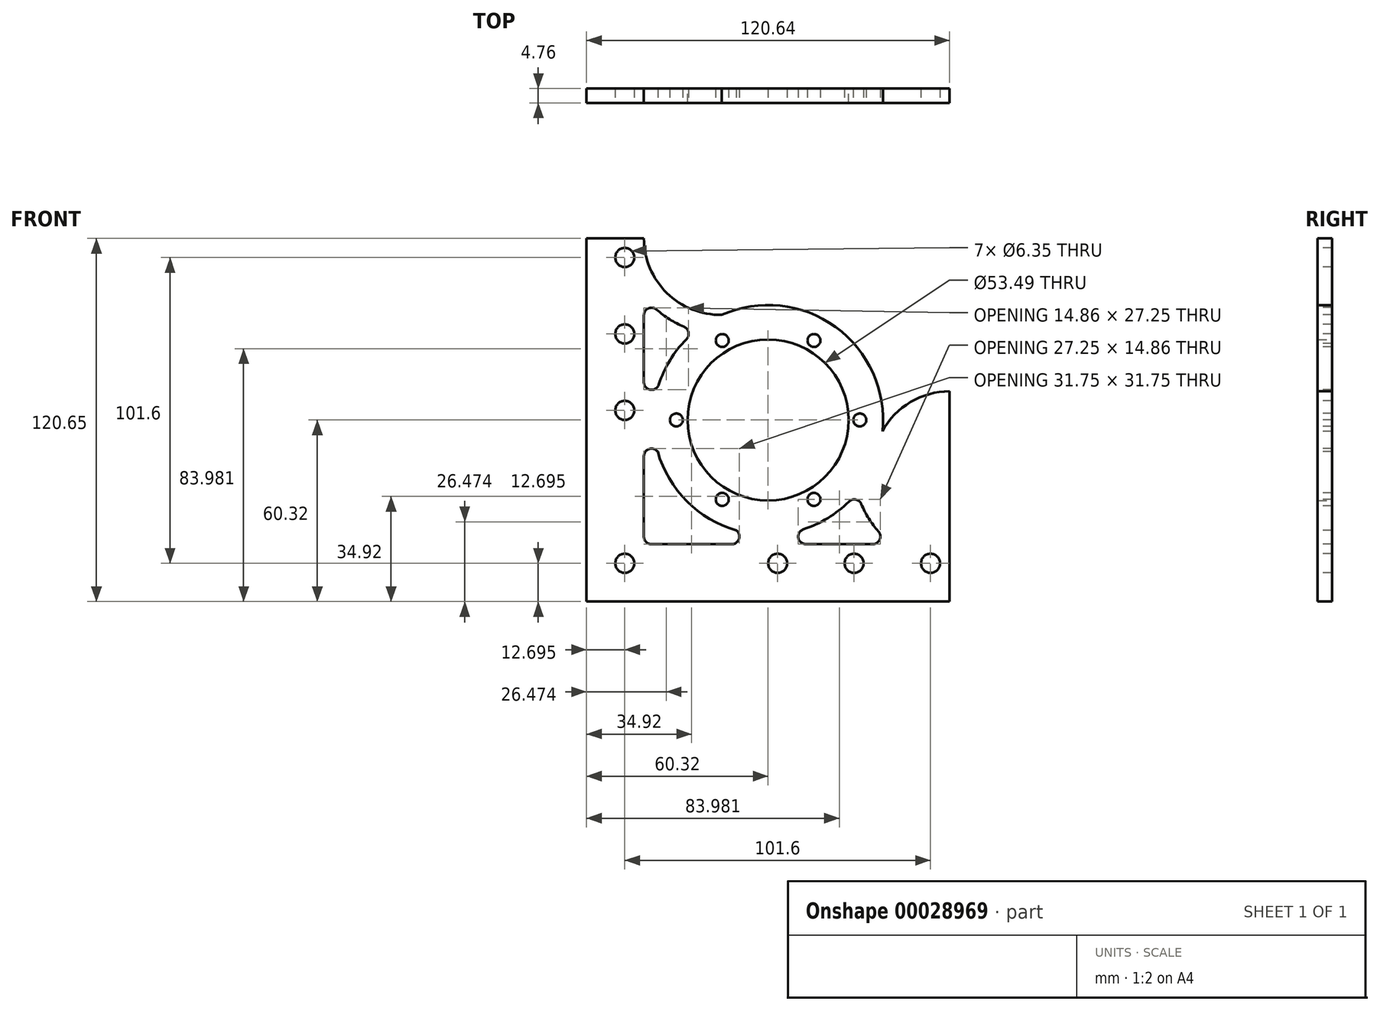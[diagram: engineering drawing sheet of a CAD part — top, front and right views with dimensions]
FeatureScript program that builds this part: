
annotation { "Feature Type Name" : "Feature", "Feature Type Description" : "" }
export const myFeature = defineFeature(function(context is Context, id is Id, definition is map)
    precondition{}
    {
        {
            var Q0;
            Q0=qCreatedBy(makeId("Front.planeOp"),FACE);
            var sketch = newSketch(context, id + "F0", { "sketchPlane" : qUnion([Q0])});
            skLineSegment(sketch, "E0.rect.bottom", {"start": v(60.32, -60.33) * mm, "end": v(-60.33, -60.33) * mm});
            skLineSegment(sketch, "E0.rect.top", {"start": v(60.33, 60.33) * mm, "end": v(-60.32, 60.33) * mm});
            skLineSegment(sketch, "E0.rect.left", {"start": v(60.32, -60.33) * mm, "end": v(60.33, 60.32) * mm});
            skLineSegment(sketch, "E0.rect.right", {"start": v(-60.33, -60.33) * mm, "end": v(-60.32, 60.32) * mm});
            skPoint(sketch, "E0.rect.middle", {"position": v(0, 0) * mm});
            skCircle(sketch, "E1", {"center": v(0, 0) * mm, "radius": 26.75 * mm});
            skSolve(sketch);
        }
        {
            var Q0;
            Q0=makeQuery(id+"F0.imprint","IMPRINT",FACE,{"disambiguationData":[TD([[makeQuery(id+"F0.imprint","IMPRINT",EDGE,{"derivedFrom":sQuery(id+"F0.wireOp",EDGE,"E0.rect.bottom")}),-1.0]])]});
            extrude(context, id + "F1", {"entities" : qUnion([Q0]), "depth" : 4.76 * mm});
        }
        {
            var Q0;
            Q0=makeQuery(id+"F1.opExtrude","CAP_FACE",FACE,{"disambiguationData":[OSD([sQuery(id+"F0.wireOp",EDGE,"E0.rect.bottom"),sQuery(id+"F0.wireOp",EDGE,"E0.rect.top"),sQuery(id+"F0.wireOp",EDGE,"E0.rect.left"),sQuery(id+"F0.wireOp",EDGE,"E0.rect.right"),sQuery(id+"F0.wireOp",EDGE,"E1")])],"isStart":false});
            var sketch = newSketch(context, id + "F2", { "sketchPlane" : qUnion([Q0])});
            skLineSegment(sketch, "E2", {"start": v(-47.63, 77.95) * mm, "end": v(-47.63, -81.86) * mm});
            skLineSegment(sketch, "E3", {"start": v(-79.01, -47.63) * mm, "end": v(89.4, -47.63) * mm});
            skPoint(sketch, "E4", {"position": v(-47.63, -47.63) * mm});
            skPoint(sketch, "E5", {"position": v(3.17, -47.63) * mm});
            skPoint(sketch, "E6", {"position": v(28.58, -47.63) * mm});
            skPoint(sketch, "E7", {"position": v(53.98, -47.63) * mm});
            skPoint(sketch, "E8", {"position": v(-47.63, 3.17) * mm});
            skPoint(sketch, "E9", {"position": v(-47.63, 28.57) * mm});
            skPoint(sketch, "E10", {"position": v(-47.63, 53.97) * mm});
            skSolve(sketch);
        }
        {
            var Q0;
            Q0=sQuery(id+"F2.wireOp",VERTEX,"E10");
            var Q1;
            Q1=sQuery(id+"F2.wireOp",VERTEX,"E9");
            var Q2;
            Q2=sQuery(id+"F2.wireOp",VERTEX,"E8");
            var Q3;
            Q3=sQuery(id+"F2.wireOp",VERTEX,"E4");
            var Q4;
            Q4=sQuery(id+"F2.wireOp",VERTEX,"E5");
            var Q5;
            Q5=sQuery(id+"F2.wireOp",VERTEX,"E6");
            var Q6;
            Q6=sQuery(id+"F2.wireOp",VERTEX,"E7");
            var Q7;
            Q7=makeQuery(id+"F1.opExtrude","SWEPT_BODY",BODY,{"disambiguationData":[OSD([sQuery(id+"F0.wireOp",EDGE,"E0.rect.bottom"),sQuery(id+"F0.wireOp",EDGE,"E0.rect.top"),sQuery(id+"F0.wireOp",EDGE,"E0.rect.left"),sQuery(id+"F0.wireOp",EDGE,"E0.rect.right"),sQuery(id+"F0.wireOp",EDGE,"E1")])]});
            hole(context, id + "F3", {"style" : HoleStyle.SIMPLE, "holeDiameter" : 6.35 * mm, "endStyle" : HoleEndStyle.THROUGH, "locations" : qUnion([Q0, Q1, Q2, Q3, Q4, Q5, Q6]), "scope" : qUnion([Q7])});
        }
        {
            var Q0;
            Q0=makeQuery(id+"F1.opExtrude","CAP_FACE",FACE,{"disambiguationData":[OSD([sQuery(id+"F0.wireOp",EDGE,"E0.rect.bottom"),sQuery(id+"F0.wireOp",EDGE,"E0.rect.top"),sQuery(id+"F0.wireOp",EDGE,"E0.rect.left"),sQuery(id+"F0.wireOp",EDGE,"E0.rect.right"),sQuery(id+"F0.wireOp",EDGE,"E1")])],"isStart":false});
            var sketch = newSketch(context, id + "F4", { "sketchPlane" : qUnion([Q0])});
            skCircle(sketch, "E11", {"center": v(0, 0) * mm, "radius": 30.48 * mm});
            skCircle(sketch, "E12.cCircle", {"center": v(0, 0) * mm, "radius": 30.48 * mm, "construction": true});
            skLineSegment(sketch, "E12.0", {"start": v(30.48, 0) * mm, "end": v(15.24, -26.4) * mm});
            skLineSegment(sketch, "E12.1", {"start": v(15.24, -26.4) * mm, "end": v(-15.24, -26.4) * mm});
            skLineSegment(sketch, "E12.2", {"start": v(-15.24, -26.4) * mm, "end": v(-30.48, 0) * mm});
            skLineSegment(sketch, "E12.3", {"start": v(-30.48, 0) * mm, "end": v(-15.24, 26.4) * mm});
            skLineSegment(sketch, "E12.4", {"start": v(-15.24, 26.4) * mm, "end": v(15.24, 26.4) * mm});
            skLineSegment(sketch, "E12.5", {"start": v(15.24, 26.4) * mm, "end": v(30.48, 0) * mm});
            skSolve(sketch);
        }
        {
            var Q0;
            Q0=sQuery(id+"F4.wireOp",VERTEX,"E12.4.end");
            var Q1;
            Q1=sQuery(id+"F4.wireOp",VERTEX,"E12.5.end");
            var Q2;
            Q2=sQuery(id+"F4.wireOp",VERTEX,"E12.0.end");
            var Q3;
            Q3=sQuery(id+"F4.wireOp",VERTEX,"E12.1.end");
            var Q4;
            Q4=sQuery(id+"F4.wireOp",VERTEX,"E12.2.end");
            var Q5;
            Q5=sQuery(id+"F4.wireOp",VERTEX,"E12.3.end");
            var Q6;
            Q6=makeQuery(id+"F1.opExtrude","SWEPT_BODY",BODY,{"disambiguationData":[OSD([sQuery(id+"F0.wireOp",EDGE,"E0.rect.bottom"),sQuery(id+"F0.wireOp",EDGE,"E0.rect.top"),sQuery(id+"F0.wireOp",EDGE,"E0.rect.left"),sQuery(id+"F0.wireOp",EDGE,"E0.rect.right"),sQuery(id+"F0.wireOp",EDGE,"E1")])]});
            hole(context, id + "F5", {"style" : HoleStyle.SIMPLE, "holeDiameter" : 4.3 * mm, "endStyle" : HoleEndStyle.THROUGH, "locations" : qUnion([Q0, Q1, Q2, Q3, Q4, Q5]), "scope" : qUnion([Q6])});
        }
        {
            var Q0;
            Q0=makeQuery(id+"F1.opExtrude","CAP_FACE",FACE,{"disambiguationData":[OSD([sQuery(id+"F0.wireOp",EDGE,"E0.rect.bottom"),sQuery(id+"F0.wireOp",EDGE,"E0.rect.top"),sQuery(id+"F0.wireOp",EDGE,"E0.rect.left"),sQuery(id+"F0.wireOp",EDGE,"E0.rect.right"),sQuery(id+"F0.wireOp",EDGE,"E1")])],"isStart":false});
            var sketch = newSketch(context, id + "F6", { "sketchPlane" : qUnion([Q0])});
            skLineSegment(sketch, "E13.0", {"start": v(-41.28, -41.28) * mm, "end": v(41.28, -41.28) * mm});
            skLineSegment(sketch, "E13.1", {"start": v(-41.28, 41.28) * mm, "end": v(-41.28, -41.28) * mm});
            skLineSegment(sketch, "E13.2", {"start": v(41.28, 41.28) * mm, "end": v(-41.28, 41.28) * mm});
            skLineSegment(sketch, "E13.3", {"start": v(41.28, -41.28) * mm, "end": v(41.28, 41.28) * mm});
            skCircle(sketch, "E14.0", {"center": v(0, 0) * mm, "radius": 38.18 * mm});
            skArc(sketch, "E15", {"start": v(-3.78, 37.99) * mm, "mid": v(-22.34, 84.89) * mm, "end": v(-15.4, 34.93) * mm});
            skArc(sketch, "E16", {"start": v(34.93, -15.4) * mm, "mid": v(84.89, -22.34) * mm, "end": v(37.99, -3.78) * mm});
            skSolve(sketch);
        }
        {
            var Q0;
            {var subQ1=sQuery(id+"F6.wireOp",EDGE,"E15");var subQ4=sQuery(id+"F6.wireOp",EDGE,"E13.2");var subQ6=makeQuery(id+"F6.imprint","INTERSECT",VERTEX,{"disambiguationData":[OD(0.0)],"derivedFrom":[subQ4,subQ1]});Q0=makeQuery(id+"F6.imprint","IMPRINT",FACE,{"disambiguationData":[TD([[makeQuery(id+"F6.imprint","IMPRINT",EDGE,{"disambiguationData":[TD([[subQ6,-1.0]])],"derivedFrom":subQ4}),-1.0]])]});}
            var Q1;
            {var subQ1=sQuery(id+"F6.wireOp",EDGE,"E13.3");var subQ6=sQuery(id+"F6.wireOp",EDGE,"E13.2");var subQ9=makeQuery(id+"F6.imprint","INTERSECT",VERTEX,{"derivedFrom":[subQ6,subQ1]});Q1=makeQuery(id+"F6.imprint","IMPRINT",FACE,{"disambiguationData":[TD([[makeQuery(id+"F6.imprint","IMPRINT",EDGE,{"disambiguationData":[TD([[subQ9,-1.0]])],"derivedFrom":subQ6}),1.0]])]});}
            var Q2;
            {var subQ1=sQuery(id+"F6.wireOp",EDGE,"E16");var subQ4=sQuery(id+"F6.wireOp",EDGE,"E13.3");var subQ6=makeQuery(id+"F6.imprint","INTERSECT",VERTEX,{"disambiguationData":[OD(0.0)],"derivedFrom":[subQ4,subQ1]});Q2=makeQuery(id+"F6.imprint","IMPRINT",FACE,{"disambiguationData":[TD([[makeQuery(id+"F6.imprint","IMPRINT",EDGE,{"disambiguationData":[TD([[subQ6,-1.0]])],"derivedFrom":subQ4}),-1.0]])]});}
            var Q3;
            {var subQ7=sQuery(id+"F6.wireOp",EDGE,"E13.3");var subQ9=sQuery(id+"F6.wireOp",EDGE,"E13.2");var subQ11=makeQuery(id+"F6.imprint","INTERSECT",VERTEX,{"derivedFrom":[subQ9,subQ7]});Q3=makeQuery(id+"F6.imprint","IMPRINT",FACE,{"disambiguationData":[TD([[makeQuery(id+"F6.imprint","IMPRINT",EDGE,{"disambiguationData":[TD([[subQ11,-1.0]])],"derivedFrom":subQ9}),-1.0]])]});}
            var Q4;
            {var subQ0=makeQuery(id+"F1.opExtrude","CAP_EDGE",EDGE,{"disambiguationData":[OSD([sQuery(id+"F0.wireOp",EDGE,"E0.rect.left")])],"isStart":false});var subQ1=sQuery(id+"F6.wireOp",EDGE,"E16");var subQ3=makeQuery(id+"F6.imprint","INTERSECT",VERTEX,{"disambiguationData":[OD(0.0)],"derivedFrom":[subQ0,subQ1]});Q4=makeQuery(id+"F6.imprint","IMPRINT",FACE,{"disambiguationData":[TD([[makeQuery(id+"F6.imprint","IMPRINT",EDGE,{"disambiguationData":[TD([[subQ3,-1.0]])],"derivedFrom":subQ1}),1.0]])]});}
            var Q5;
            {var subQ0=makeQuery(id+"F1.opExtrude","CAP_EDGE",EDGE,{"disambiguationData":[OSD([sQuery(id+"F0.wireOp",EDGE,"E0.rect.top")])],"isStart":false});var subQ1=sQuery(id+"F6.wireOp",EDGE,"E15");var subQ3=makeQuery(id+"F6.imprint","INTERSECT",VERTEX,{"disambiguationData":[OD(0.0)],"derivedFrom":[subQ0,subQ1]});Q5=makeQuery(id+"F6.imprint","IMPRINT",FACE,{"disambiguationData":[TD([[makeQuery(id+"F6.imprint","IMPRINT",EDGE,{"disambiguationData":[TD([[subQ3,-1.0]])],"derivedFrom":subQ1}),1.0]])]});}
            var Q6;
            {var subQ0=sQuery(id+"F6.wireOp",EDGE,"E16");var subQ1=sQuery(id+"F6.wireOp",EDGE,"E13.3");var subQ2=makeQuery(id+"F6.imprint","INTERSECT",VERTEX,{"disambiguationData":[OD(0.0)],"derivedFrom":[subQ1,subQ0]});Q6=makeQuery(id+"F6.imprint","IMPRINT",FACE,{"disambiguationData":[TD([[makeQuery(id+"F6.imprint","IMPRINT",EDGE,{"disambiguationData":[TD([[subQ2,-1.0]])],"derivedFrom":subQ1}),1.0]])]});}
            var Q7;
            {var subQ0=sQuery(id+"F6.wireOp",EDGE,"E15");var subQ1=sQuery(id+"F6.wireOp",EDGE,"E13.2");var subQ5=makeQuery(id+"F6.imprint","INTERSECT",VERTEX,{"disambiguationData":[OD(0.0)],"derivedFrom":[subQ1,subQ0]});Q7=makeQuery(id+"F6.imprint","IMPRINT",FACE,{"disambiguationData":[TD([[makeQuery(id+"F6.imprint","IMPRINT",EDGE,{"disambiguationData":[TD([[subQ5,-1.0]])],"derivedFrom":subQ1}),1.0]])]});}
            extrude(context, id + "F7", {"entities" : qUnion([Q0, Q1, Q2, Q3, Q4, Q5, Q6, Q7]), "operationType" : NewBodyOperationType.REMOVE, "oppositeDirection" : true, "depth" : 25.4 * mm});
        }
        {
            var Q0;
            Q0=makeQuery(id+"F1.opExtrude","CAP_FACE",FACE,{"disambiguationData":[OSD([sQuery(id+"F0.wireOp",EDGE,"E0.rect.bottom"),sQuery(id+"F0.wireOp",EDGE,"E0.rect.top"),sQuery(id+"F0.wireOp",EDGE,"E0.rect.left"),sQuery(id+"F0.wireOp",EDGE,"E0.rect.right"),sQuery(id+"F0.wireOp",EDGE,"E1")])],"isStart":false});
            var sketch = newSketch(context, id + "F8", { "sketchPlane" : qUnion([Q0])});
            skLineSegment(sketch, "E17.0", {"start": v(-41.28, -41.28) * mm, "end": v(-41.27, 60.32) * mm});
            skLineSegment(sketch, "E17.1", {"start": v(60.32, -41.28) * mm, "end": v(-41.28, -41.28) * mm});
            skArc(sketch, "E18.0", {"start": v(28.64, -13.89) * mm, "mid": v(22.5, 22.5) * mm, "end": v(-13.89, 28.64) * mm});
            skArc(sketch, "E18.1", {"start": v(53.98, -46.98) * mm, "mid": v(35.11, -35.17) * mm, "end": v(28.64, -13.89) * mm});
            skLineSegment(sketch, "E18.2", {"start": v(53.98, -53.98) * mm, "end": v(53.98, -46.98) * mm});
            skLineSegment(sketch, "E18.3", {"start": v(-53.98, -53.98) * mm, "end": v(53.98, -53.98) * mm});
            skLineSegment(sketch, "E18.4", {"start": v(-53.98, 53.98) * mm, "end": v(-53.98, -53.98) * mm});
            skArc(sketch, "E18.5", {"start": v(-13.89, 28.64) * mm, "mid": v(-35.17, 35.11) * mm, "end": v(-46.98, 53.98) * mm});
            skLineSegment(sketch, "E18.6", {"start": v(-46.98, 53.98) * mm, "end": v(-53.98, 53.98) * mm});
            skCircle(sketch, "E19.0", {"center": v(0, 0) * mm, "radius": 38.18 * mm});
            skCircle(sketch, "E20", {"center": v(-38.74, -12.07) * mm, "radius": 2.54 * mm});
            skCircle(sketch, "E21", {"center": v(-12.07, -38.74) * mm, "radius": 2.54 * mm});
            skCircle(sketch, "E22", {"center": v(12.55, -38.74) * mm, "radius": 2.54 * mm});
            skCircle(sketch, "E23", {"center": v(28.63, -28.95) * mm, "radius": 2.54 * mm});
            skCircle(sketch, "E24", {"center": v(-28.95, 28.63) * mm, "radius": 2.54 * mm});
            skCircle(sketch, "E25", {"center": v(-38.74, 12.55) * mm, "radius": 2.54 * mm});
            skCircle(sketch, "E26", {"center": v(-38.74, 34.77) * mm, "radius": 2.54 * mm});
            skCircle(sketch, "E27", {"center": v(34.77, -38.74) * mm, "radius": 2.54 * mm});
            skCircle(sketch, "E28", {"center": v(-38.74, -38.74) * mm, "radius": 2.54 * mm});
            skSolve(sketch);
        }
        {
            var Q0;
            {var subQ3=sQuery(id+"F8.wireOp",EDGE,"E17.0");var subQ5=sQuery(id+"F8.wireOp",EDGE,"E25");var subQ8=makeQuery(id+"F8.imprint","INTERSECT",VERTEX,{"derivedFrom":[subQ3,subQ5]});Q0=makeQuery(id+"F8.imprint","IMPRINT",FACE,{"disambiguationData":[TD([[makeQuery(id+"F8.imprint","IMPRINT",EDGE,{"disambiguationData":[TD([[subQ8,-1.0]])],"derivedFrom":subQ3}),-1.0]])]});}
            var Q1;
            {var subQ0=sQuery(id+"F8.wireOp",EDGE,"E26");var subQ2=makeQuery(id+"F8.imprint","INTERSECT",VERTEX,{"derivedFrom":[sQuery(id+"F8.wireOp",EDGE,"E17.0"),subQ0]});Q1=makeQuery(id+"F8.imprint","IMPRINT",FACE,{"disambiguationData":[TD([[makeQuery(id+"F8.imprint","IMPRINT",EDGE,{"disambiguationData":[TD([[subQ2,1.0]])],"derivedFrom":subQ0}),1.0]])]});}
            var Q2;
            {var subQ0=sQuery(id+"F8.wireOp",EDGE,"E24");var subQ2=makeQuery(id+"F8.imprint","INTERSECT",VERTEX,{"derivedFrom":[sQuery(id+"F8.wireOp",EDGE,"E19.0"),subQ0]});Q2=makeQuery(id+"F8.imprint","IMPRINT",FACE,{"disambiguationData":[TD([[makeQuery(id+"F8.imprint","IMPRINT",EDGE,{"disambiguationData":[TD([[subQ2,1.0]])],"derivedFrom":subQ0}),1.0]])]});}
            var Q3;
            {var subQ0=sQuery(id+"F8.wireOp",EDGE,"E25");var subQ2=makeQuery(id+"F8.imprint","INTERSECT",VERTEX,{"derivedFrom":[sQuery(id+"F8.wireOp",EDGE,"E17.0"),subQ0]});Q3=makeQuery(id+"F8.imprint","IMPRINT",FACE,{"disambiguationData":[TD([[makeQuery(id+"F8.imprint","IMPRINT",EDGE,{"disambiguationData":[TD([[subQ2,-1.0]])],"derivedFrom":subQ0}),1.0]])]});}
            var Q4;
            {var subQ0=sQuery(id+"F8.wireOp",EDGE,"E20");var subQ1=sQuery(id+"F8.wireOp",EDGE,"E19.0");var subQ4=makeQuery(id+"F8.imprint","INTERSECT",VERTEX,{"disambiguationData":[OD(0.0)],"derivedFrom":[subQ1,subQ0]});Q4=makeQuery(id+"F8.imprint","IMPRINT",FACE,{"disambiguationData":[TD([[makeQuery(id+"F8.imprint","IMPRINT",EDGE,{"disambiguationData":[TD([[subQ4,-1.0]])],"derivedFrom":subQ1}),-1.0]])]});}
            var Q5;
            {var subQ0=sQuery(id+"F8.wireOp",EDGE,"E28");var subQ2=makeQuery(id+"F8.imprint","INTERSECT",VERTEX,{"derivedFrom":[sQuery(id+"F8.wireOp",EDGE,"E17.0"),subQ0]});Q5=makeQuery(id+"F8.imprint","IMPRINT",FACE,{"disambiguationData":[TD([[makeQuery(id+"F8.imprint","IMPRINT",EDGE,{"disambiguationData":[TD([[subQ2,-1.0]])],"derivedFrom":subQ0}),1.0]])]});}
            var Q6;
            {var subQ0=sQuery(id+"F8.wireOp",EDGE,"E21");var subQ1=sQuery(id+"F8.wireOp",EDGE,"E19.0");var subQ4=makeQuery(id+"F8.imprint","INTERSECT",VERTEX,{"disambiguationData":[OD(0.0)],"derivedFrom":[subQ1,subQ0]});Q6=makeQuery(id+"F8.imprint","IMPRINT",FACE,{"disambiguationData":[TD([[makeQuery(id+"F8.imprint","IMPRINT",EDGE,{"disambiguationData":[TD([[subQ4,-1.0]])],"derivedFrom":subQ1}),-1.0]])]});}
            var Q7;
            {var subQ0=sQuery(id+"F8.wireOp",EDGE,"E28");var subQ3=sQuery(id+"F8.wireOp",EDGE,"E17.0");var subQ4=makeQuery(id+"F8.imprint","INTERSECT",VERTEX,{"derivedFrom":[subQ3,subQ0]});Q7=makeQuery(id+"F8.imprint","IMPRINT",FACE,{"disambiguationData":[TD([[makeQuery(id+"F8.imprint","IMPRINT",EDGE,{"disambiguationData":[TD([[subQ4,-1.0]])],"derivedFrom":subQ3}),-1.0]])]});}
            var Q8;
            {var subQ0=sQuery(id+"F8.wireOp",EDGE,"E27");var subQ3=sQuery(id+"F8.wireOp",EDGE,"E17.1");var subQ4=makeQuery(id+"F8.imprint","INTERSECT",VERTEX,{"derivedFrom":[subQ3,subQ0]});Q8=makeQuery(id+"F8.imprint","IMPRINT",FACE,{"disambiguationData":[TD([[makeQuery(id+"F8.imprint","IMPRINT",EDGE,{"disambiguationData":[TD([[subQ4,-1.0]])],"derivedFrom":subQ3}),-1.0]])]});}
            var Q9;
            {var subQ0=sQuery(id+"F8.wireOp",EDGE,"E23");var subQ2=makeQuery(id+"F8.imprint","INTERSECT",VERTEX,{"derivedFrom":[sQuery(id+"F8.wireOp",EDGE,"E19.0"),subQ0]});Q9=makeQuery(id+"F8.imprint","IMPRINT",FACE,{"disambiguationData":[TD([[makeQuery(id+"F8.imprint","IMPRINT",EDGE,{"disambiguationData":[TD([[subQ2,1.0]])],"derivedFrom":subQ0}),1.0]])]});}
            var Q10;
            {var subQ0=sQuery(id+"F8.wireOp",EDGE,"E27");var subQ2=makeQuery(id+"F8.imprint","INTERSECT",VERTEX,{"derivedFrom":[sQuery(id+"F8.wireOp",EDGE,"E17.1"),subQ0]});Q10=makeQuery(id+"F8.imprint","IMPRINT",FACE,{"disambiguationData":[TD([[makeQuery(id+"F8.imprint","IMPRINT",EDGE,{"disambiguationData":[TD([[subQ2,1.0]])],"derivedFrom":subQ0}),1.0]])]});}
            var Q11;
            {var subQ0=sQuery(id+"F8.wireOp",EDGE,"E22");var subQ2=makeQuery(id+"F8.imprint","INTERSECT",VERTEX,{"derivedFrom":[sQuery(id+"F8.wireOp",EDGE,"E17.1"),subQ0]});Q11=makeQuery(id+"F8.imprint","IMPRINT",FACE,{"disambiguationData":[TD([[makeQuery(id+"F8.imprint","IMPRINT",EDGE,{"disambiguationData":[TD([[subQ2,1.0]])],"derivedFrom":subQ0}),1.0]])]});}
            extrude(context, id + "F9", {"entities" : qUnion([Q0, Q1, Q2, Q3, Q4, Q5, Q6, Q7, Q8, Q9, Q10, Q11]), "operationType" : NewBodyOperationType.REMOVE, "oppositeDirection" : true, "depth" : 25.4 * mm});
        }
    });
